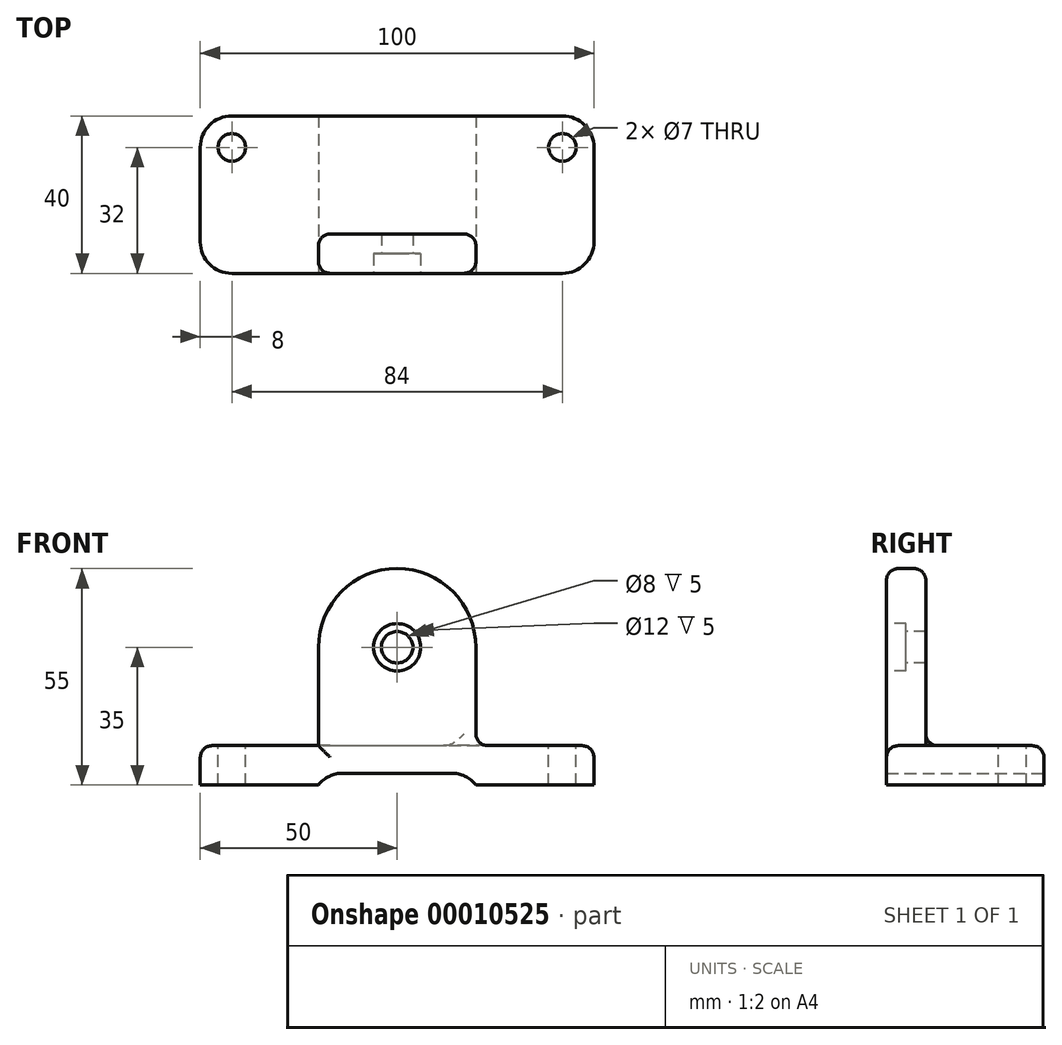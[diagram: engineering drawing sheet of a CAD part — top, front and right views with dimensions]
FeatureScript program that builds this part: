
annotation { "Feature Type Name" : "Feature", "Feature Type Description" : "" }
export const myFeature = defineFeature(function(context is Context, id is Id, definition is map)
    precondition{}
    {
        {
            var Q0;
            Q0=qCreatedBy(makeId("Top.planeOp"),FACE);
            var sketch = newSketch(context, id + "F0", { "sketchPlane" : qUnion([Q0])});
            skLineSegment(sketch, "E0.bottom", {"start": v(0, 0) * mm, "end": v(100, 0) * mm});
            skLineSegment(sketch, "E0.top", {"start": v(0, 40) * mm, "end": v(100, 40) * mm});
            skLineSegment(sketch, "E0.left", {"start": v(0, 0) * mm, "end": v(0, 40) * mm});
            skLineSegment(sketch, "E0.right", {"start": v(100, 0) * mm, "end": v(100, 40) * mm});
            skSolve(sketch);
        }
        {
            var Q0;
            Q0 = qSketchRegion(id + "F0", true);
            extrude(context, id + "F1", {"entities" : qUnion([Q0]), "depth" : 10 * mm});
        }
        {
            var Q0;
            Q0=makeQuery(id+"F1.opExtrude","SWEPT_FACE",FACE,{"disambiguationData":[OSD([sQuery(id+"F0.wireOp",EDGE,"E0.bottom")])]});
            var sketch = newSketch(context, id + "F2", { "sketchPlane" : qUnion([Q0])});
            skLineSegment(sketch, "E1", {"start": v(30, 0) * mm, "end": v(30, 35) * mm});
            skArc(sketch, "E2", {"start": v(30, 35) * mm, "mid": v(50, 55) * mm, "end": v(70, 35) * mm});
            skLineSegment(sketch, "E3", {"start": v(70, 35) * mm, "end": v(70, 0) * mm});
            skLineSegment(sketch, "E4", {"start": v(70, 0) * mm, "end": v(30, 0) * mm});
            skSolve(sketch);
        }
        {
            var Q0;
            Q0 = qSketchRegion(id + "F2", true);
            extrude(context, id + "F3", {"entities" : qUnion([Q0]), "operationType" : NewBodyOperationType.ADD, "oppositeDirection" : true, "depth" : 10 * mm});
        }
        {
            var Q0;
            Q0=makeQuery(id+"F3.boolean.opBoolean","MERGE",FACE,{"derivedFrom":[makeQuery(id+"F1.opExtrude","SWEPT_FACE",FACE,{"disambiguationData":[OSD([sQuery(id+"F0.wireOp",EDGE,"E0.bottom")])]}),makeQuery(id+"F3.opExtrude","CAP_FACE",FACE,{"disambiguationData":[OSD([sQuery(id+"F2.wireOp",EDGE,"E1"),sQuery(id+"F2.wireOp",EDGE,"E2"),sQuery(id+"F2.wireOp",EDGE,"E3"),sQuery(id+"F2.wireOp",EDGE,"E4")])],"isStart":true})]});
            var sketch = newSketch(context, id + "F4", { "sketchPlane" : qUnion([Q0])});
            skLineSegment(sketch, "E5.bottom", {"start": v(30, 0) * mm, "end": v(70, 0) * mm});
            skLineSegment(sketch, "E5.top", {"start": v(30, 3) * mm, "end": v(70, 3) * mm});
            skLineSegment(sketch, "E5.left", {"start": v(30, 0) * mm, "end": v(30, 3) * mm});
            skLineSegment(sketch, "E5.right", {"start": v(70, 0) * mm, "end": v(70, 3) * mm});
            skSolve(sketch);
        }
        {
            var Q0;
            Q0 = qSketchRegion(id + "F4", true);
            extrude(context, id + "F5", {"entities" : qUnion([Q0]), "operationType" : NewBodyOperationType.REMOVE, "endBound" : BoundingType.THROUGH_ALL, "oppositeDirection" : true, "depth" : 25 * mm});
        }
        {
            var Q0;
            Q0=makeQuery(id+"F3.boolean.opBoolean","MERGE",FACE,{"derivedFrom":[makeQuery(id+"F1.opExtrude","SWEPT_FACE",FACE,{"disambiguationData":[OSD([sQuery(id+"F0.wireOp",EDGE,"E0.bottom")])]}),makeQuery(id+"F3.opExtrude","CAP_FACE",FACE,{"disambiguationData":[OSD([sQuery(id+"F2.wireOp",EDGE,"E1"),sQuery(id+"F2.wireOp",EDGE,"E2"),sQuery(id+"F2.wireOp",EDGE,"E3"),sQuery(id+"F2.wireOp",EDGE,"E4")])],"isStart":true})]});
            var sketch = newSketch(context, id + "F6", { "sketchPlane" : qUnion([Q0])});
            skCircle(sketch, "E6", {"center": v(50, 35) * mm, "radius": 4 * mm});
            skSolve(sketch);
        }
        {
            var Q0;
            Q0=sQuery(id+"F6.wireOp",VERTEX,"E6.center");
            var Q1;
            Q1=makeQuery(id+"F1.opExtrude","SWEPT_BODY",BODY,{"disambiguationData":[OSD([sQuery(id+"F0.wireOp",EDGE,"E0.bottom"),sQuery(id+"F0.wireOp",EDGE,"E0.top"),sQuery(id+"F0.wireOp",EDGE,"E0.left"),sQuery(id+"F0.wireOp",EDGE,"E0.right")])]});
            hole(context, id + "F7", {"style" : HoleStyle.C_BORE, "endStyle" : HoleEndStyle.THROUGH, "holeDiameter" : 8 * mm, "cBoreDiameter" : 12 * mm, "cBoreDepth" : 5 * mm, "tappedDepth" : 12 * mm, "tapClearance" : 3, "locations" : qUnion([Q0]), "scope" : qUnion([Q1])});
        }
        {
            var Q0;
            Q0=makeQuery(id+"F1.opExtrude","SWEPT_EDGE",EDGE,{"disambiguationData":[OSD([sQuery(id+"F0.wireOp",EDGE,"E0.top"),sQuery(id+"F0.wireOp",EDGE,"E0.right")])]});
            var Q1;
            Q1=makeQuery(id+"F1.opExtrude","SWEPT_EDGE",EDGE,{"disambiguationData":[OSD([sQuery(id+"F0.wireOp",EDGE,"E0.bottom"),sQuery(id+"F0.wireOp",EDGE,"E0.right")])]});
            var Q2;
            Q2=makeQuery(id+"F1.opExtrude","SWEPT_EDGE",EDGE,{"disambiguationData":[OSD([sQuery(id+"F0.wireOp",EDGE,"E0.bottom"),sQuery(id+"F0.wireOp",EDGE,"E0.left")])]});
            var Q3;
            Q3=makeQuery(id+"F1.opExtrude","SWEPT_EDGE",EDGE,{"disambiguationData":[OSD([sQuery(id+"F0.wireOp",EDGE,"E0.top"),sQuery(id+"F0.wireOp",EDGE,"E0.left")])]});
            var Q4;
            Q4=makeQuery(id+"F5.boolean.opBoolean","COPY",EDGE,{"derivedFrom":makeQuery(id+"F5.opExtrude","SWEPT_EDGE",EDGE,{"disambiguationData":[OSD([sQuery(id+"F4.wireOp",EDGE,"E5.top"),sQuery(id+"F4.wireOp",EDGE,"E5.right")])]})});
            var Q5;
            Q5=makeQuery(id+"F5.boolean.opBoolean","COPY",EDGE,{"derivedFrom":makeQuery(id+"F5.opExtrude","SWEPT_EDGE",EDGE,{"disambiguationData":[OSD([sQuery(id+"F4.wireOp",EDGE,"E5.top"),sQuery(id+"F4.wireOp",EDGE,"E5.left")])]})});
            fillet(context, id + "F8", {"entities" : qUnion([Q0, Q1, Q2, Q3, Q4, Q5]), "radius" : 8 * mm, "tangentPropagation" : true, "allowEdgeOverflow" : false});
        }
        {
            var Q0;
            Q0=makeQuery(id+"F1.opExtrude","CAP_FACE",FACE,{"disambiguationData":[OSD([sQuery(id+"F0.wireOp",EDGE,"E0.bottom"),sQuery(id+"F0.wireOp",EDGE,"E0.top"),sQuery(id+"F0.wireOp",EDGE,"E0.left"),sQuery(id+"F0.wireOp",EDGE,"E0.right")])],"isStart":false});
            var sketch = newSketch(context, id + "F9", { "sketchPlane" : qUnion([Q0])});
            skPoint(sketch, "E7", {"position": v(8, 32) * mm});
            skPoint(sketch, "E8", {"position": v(8, 8) * mm});
            skPoint(sketch, "E9", {"position": v(92, 32) * mm});
            skPoint(sketch, "E10", {"position": v(92, 8) * mm});
            skSolve(sketch);
        }
        {
            var Q0;
            Q0=sQuery(id+"F9.wireOp",VERTEX,"E7");
            var Q1;
            Q1=sQuery(id+"F9.wireOp",VERTEX,"E9");
            var Q2;
            Q2=makeQuery(id+"F1.opExtrude","SWEPT_BODY",BODY,{"disambiguationData":[OSD([sQuery(id+"F0.wireOp",EDGE,"E0.bottom"),sQuery(id+"F0.wireOp",EDGE,"E0.top"),sQuery(id+"F0.wireOp",EDGE,"E0.left"),sQuery(id+"F0.wireOp",EDGE,"E0.right")])]});
            hole(context, id + "F10", {"style" : HoleStyle.SIMPLE, "endStyle" : HoleEndStyle.THROUGH, "holeDiameter" : 7 * mm, "tappedDepth" : 12 * mm, "tapClearance" : 3, "locations" : qUnion([Q0, Q1]), "scope" : qUnion([Q2])});
        }
        {
            var Q0;
            Q0=makeQuery(id+"F3.opExtrude","CAP_EDGE",EDGE,{"disambiguationData":[OSD([sQuery(id+"F2.wireOp",EDGE,"E3")])],"isStart":false});
            var Q1;
            Q1=makeQuery(id+"F3.opExtrude","CAP_EDGE",EDGE,{"disambiguationData":[OSD([sQuery(id+"F2.wireOp",EDGE,"E3")])],"isStart":true});
            var Q2;
            {var subQ1=sQuery(id+"F0.wireOp",EDGE,"E0.right");var subQ2=sQuery(id+"F0.wireOp",EDGE,"E0.bottom");Q2=makeQuery(id+"F3.boolean.opBoolean","SPLIT",EDGE,{"disambiguationData":[TD([makeQuery(id+"F1.opExtrude","SWEPT_FACE",FACE,{"disambiguationData":[OSD([subQ1])]})])],"derivedFrom":makeQuery(id+"F1.opExtrude","CAP_EDGE",EDGE,{"disambiguationData":[OSD([subQ2])],"isStart":false})});}
            var Q3;
            Q3=makeQuery(id+"F3.boolean.opBoolean","INTERSECT",EDGE,{"derivedFrom":[makeQuery(id+"F1.opExtrude","CAP_FACE",FACE,{"disambiguationData":[OSD([sQuery(id+"F0.wireOp",EDGE,"E0.bottom"),sQuery(id+"F0.wireOp",EDGE,"E0.top"),sQuery(id+"F0.wireOp",EDGE,"E0.left"),sQuery(id+"F0.wireOp",EDGE,"E0.right")])],"isStart":false}),makeQuery(id+"F3.opExtrude","SWEPT_FACE",FACE,{"disambiguationData":[OSD([sQuery(id+"F2.wireOp",EDGE,"E3")])]})]});
            fillet(context, id + "F11", {"entities" : qUnion([Q0, Q1, Q2, Q3]), "radius" : 3 * mm, "tangentPropagation" : true, "allowEdgeOverflow" : false});
        }
    });
